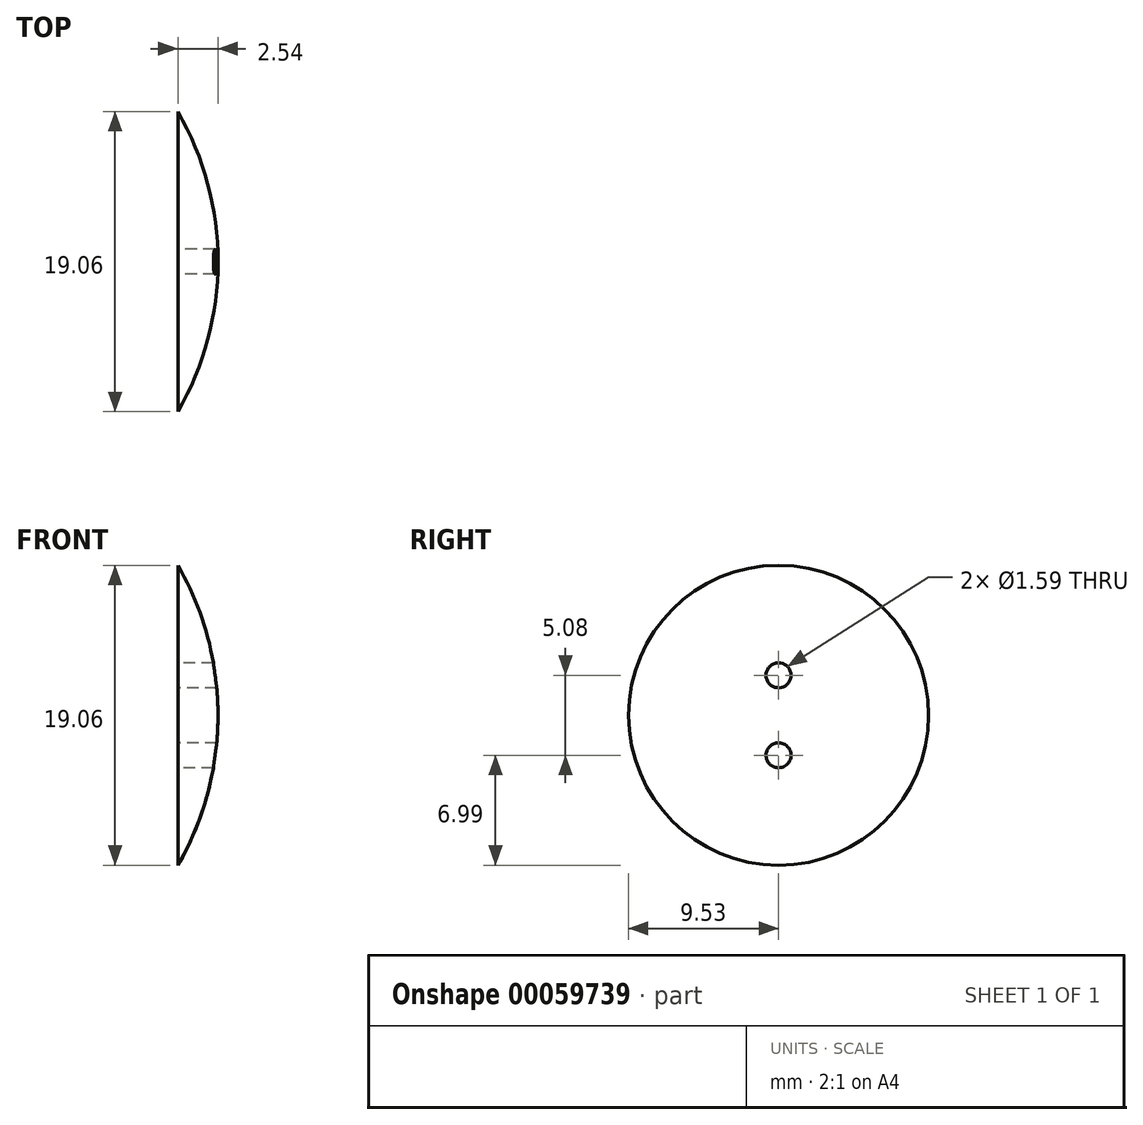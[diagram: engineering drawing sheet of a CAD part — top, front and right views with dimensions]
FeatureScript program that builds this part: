
annotation { "Feature Type Name" : "Feature", "Feature Type Description" : "" }
export const myFeature = defineFeature(function(context is Context, id is Id, definition is map)
    precondition{}
    {
        {
            var Q0;
            Q0=qCreatedBy(makeId("Front.planeOp"),FACE);
            var sketch = newSketch(context, id + "F0", { "sketchPlane" : qUnion([Q0])});
            skLineSegment(sketch, "E0", {"start": v(0, 0) * mm, "end": v(2.54, 0) * mm, "construction": true});
            skLineSegment(sketch, "E1", {"start": v(0, 0) * mm, "end": v(0, 9.53) * mm, "construction": true});
            skLineSegment(sketch, "E2", {"start": v(0, 0) * mm, "end": v(0, -9.53) * mm, "construction": true});
            skArc(sketch, "E3", {"start": v(2.54, 0) * mm, "mid": v(1.9, 4.93) * mm, "end": v(0, 9.53) * mm});
            skLineSegment(sketch, "E4", {"start": v(0, 9.53) * mm, "end": v(0, 0) * mm});
            skLineSegment(sketch, "E5", {"start": v(0, 0) * mm, "end": v(2.54, 0) * mm});
            skSolve(sketch);
        }
        {
            var Q0;
            Q0=qSketchRegion(id+"F0",true);
            var Q1;
            Q1=sQuery(id+"F0.wireOp",EDGE,"E0");
            revolve(context, id + "F1", {"entities" : qUnion([Q0]), "axis" : qUnion([Q1]), "revolveType" : RevolveType.FULL});
        }
        {
            var Q0;
            Q0=makeQuery(id+"F1.opRevolve","SWEPT_FACE",FACE,{"disambiguationData":[OSD([sQuery(id+"F0.wireOp",EDGE,"E4")])]});
            var sketch = newSketch(context, id + "F2", { "sketchPlane" : qUnion([Q0])});
            skLineSegment(sketch, "E6", {"start": v(0, 0) * mm, "end": v(0, 2.54) * mm, "construction": true});
            skLineSegment(sketch, "E7", {"start": v(0, 0) * mm, "end": v(0, -2.54) * mm, "construction": true});
            skCircle(sketch, "E8", {"center": v(0, 2.54) * mm, "radius": 0.8 * mm});
            skCircle(sketch, "E9", {"center": v(0, -2.54) * mm, "radius": 0.8 * mm});
            skSolve(sketch);
        }
        {
            var Q0;
            Q0=makeQuery(id+"F2.imprint","IMPRINT",FACE,{"disambiguationData":[TD([[makeQuery(id+"F2.imprint","IMPRINT",EDGE,{"derivedFrom":sQuery(id+"F2.wireOp",EDGE,"E8")}),1.0]])]});
            var Q1;
            Q1=makeQuery(id+"F2.imprint","IMPRINT",FACE,{"disambiguationData":[TD([[makeQuery(id+"F2.imprint","IMPRINT",EDGE,{"derivedFrom":sQuery(id+"F2.wireOp",EDGE,"E9")}),1.0]])]});
            extrude(context, id + "F3", {"entities" : qUnion([Q0, Q1]), "operationType" : NewBodyOperationType.REMOVE, "endBound" : BoundingType.THROUGH_ALL, "oppositeDirection" : true, "depth" : 25.4 * mm});
        }
    });
